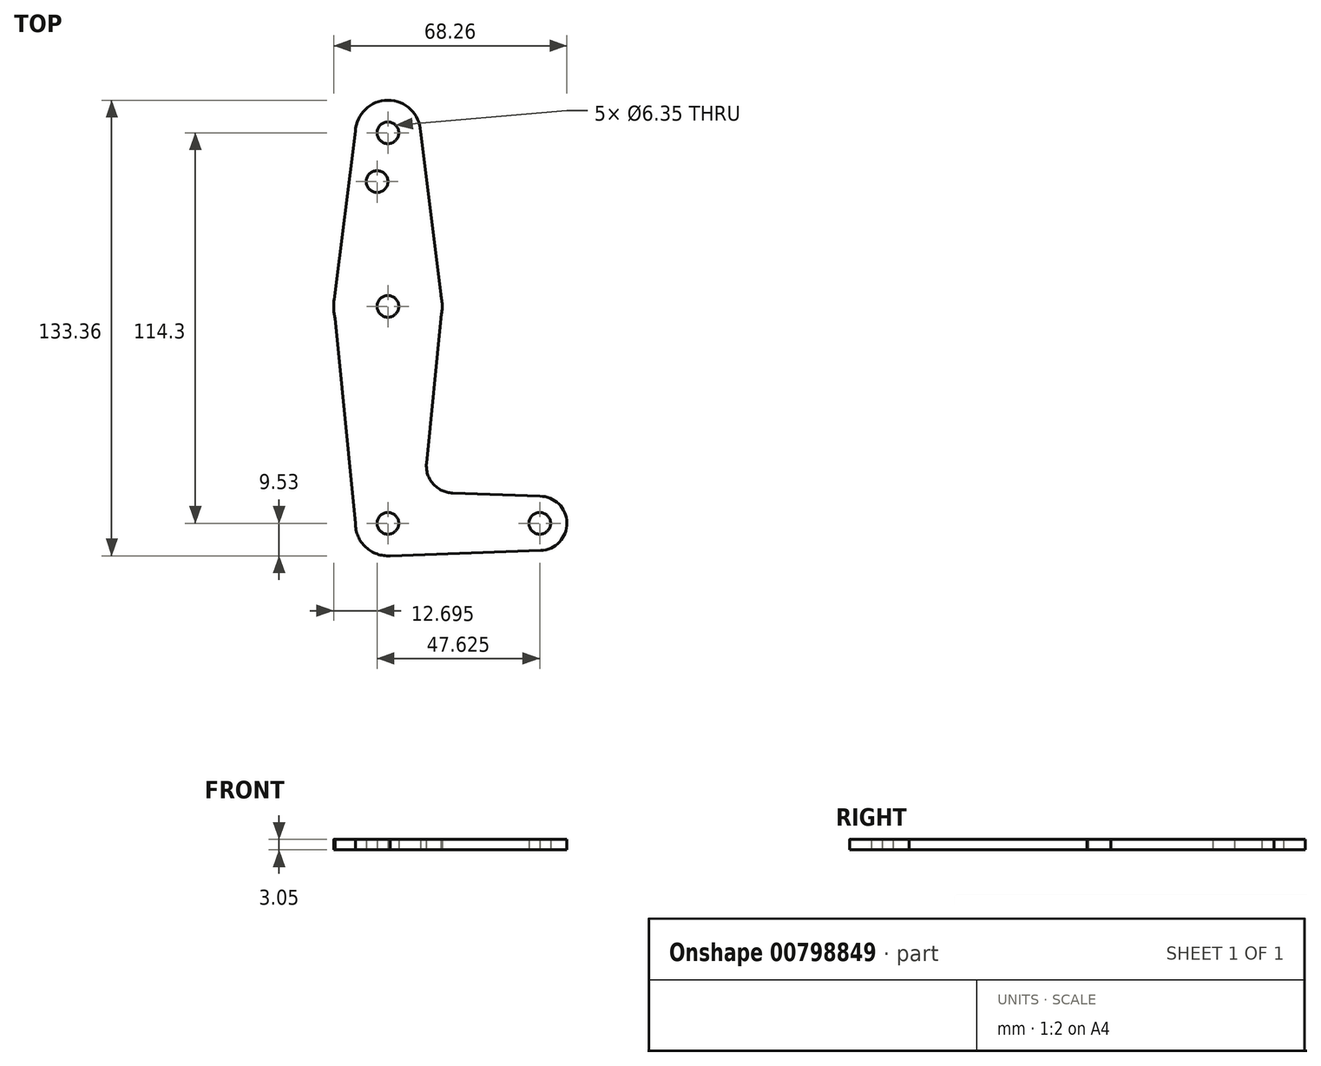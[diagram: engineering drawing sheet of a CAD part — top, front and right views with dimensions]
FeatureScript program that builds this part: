
annotation { "Feature Type Name" : "Feature", "Feature Type Description" : "" }
export const myFeature = defineFeature(function(context is Context, id is Id, definition is map)
    precondition{}
    {
        {
            var Q0;
            Q0=qCreatedBy(makeId("Top.planeOp"),FACE);
            var sketch = newSketch(context, id + "F0", { "sketchPlane" : qUnion([Q0])});
            skCircle(sketch, "E0", {"center": v(0, 0) * mm, "radius": 9.53 * mm});
            skLineSegment(sketch, "E1", {"start": v(0, 0) * mm, "end": v(0, 114.3) * mm});
            skCircle(sketch, "E2", {"center": v(0, 114.3) * mm, "radius": 9.53 * mm});
            skCircle(sketch, "E3", {"center": v(0, 63.5) * mm, "radius": 15.88 * mm});
            skLineSegment(sketch, "E4", {"start": v(0, 0) * mm, "end": v(44.45, 0) * mm});
            skCircle(sketch, "E5", {"center": v(44.45, 0) * mm, "radius": 7.94 * mm});
            skLineSegment(sketch, "E6", {"start": v(0, -9.53) * mm, "end": v(44.73, -7.93) * mm});
            skLineSegment(sketch, "E7", {"start": v(44.45, 7.94) * mm, "end": v(18.93, 8.85) * mm});
            skLineSegment(sketch, "E8", {"start": v(15.87, 63.92) * mm, "end": v(11.3, 17.58) * mm});
            skLineSegment(sketch, "E9", {"start": v(9.52, 114.67) * mm, "end": v(15.87, 63.92) * mm});
            skCircle(sketch, "E10", {"center": v(0, 114.3) * mm, "radius": 3.18 * mm});
            skCircle(sketch, "E11", {"center": v(44.45, 0) * mm, "radius": 3.18 * mm});
            skCircle(sketch, "E12", {"center": v(0, 0) * mm, "radius": 3.18 * mm});
            skCircle(sketch, "E13", {"center": v(0, 63.5) * mm, "radius": 3.18 * mm});
            skLineSegment(sketch, "E14", {"start": v(0, 100.03) * mm, "end": v(-3.18, 100.03) * mm});
            skCircle(sketch, "E15", {"center": v(-3.18, 100.03) * mm, "radius": 3.18 * mm});
            skPoint(sketch, "E16.newPointA", {"position": v(9.57, 0) * mm});
            skPoint(sketch, "E16.newPointB", {"position": v(0, 9.53) * mm});
            skArc(sketch, "E16.filletArc", {"start": v(11.3, 17.58) * mm, "mid": v(13.23, 11.57) * mm, "end": v(18.93, 8.85) * mm});
            skLineSegment(sketch, "E17", {"start": v(-9.52, 114.72) * mm, "end": v(-15.75, 65.5) * mm});
            skLineSegment(sketch, "E18", {"start": v(-9.53, 0) * mm, "end": v(-15.5, 60.08) * mm});
            skSolve(sketch);
        }
        {
            var Q0;
            Q0 = qSketchRegion(id + "F0", true);
            var Q1;
            {var subQ0=sQuery(id+"F0.wireOp",EDGE,"E1");var subQ1=sQuery(id+"F0.wireOp",EDGE,"E0");var subQ2=makeQuery(id+"F0.imprint","INTERSECT",VERTEX,{"derivedFrom":[subQ1,subQ0]});Q1=makeQuery(id+"F0.imprint","IMPRINT",FACE,{"disambiguationData":[TD([[makeQuery(id+"F0.imprint","IMPRINT",EDGE,{"disambiguationData":[TD([[subQ2,1.0]])],"derivedFrom":subQ1}),1.0]])]});}
            extrude(context, id + "F1", {"entities" : qUnion([Q0, Q1]), "depth" : 3.05 * mm, "offsetDistance" : 25.4 * mm});
        }
    });
